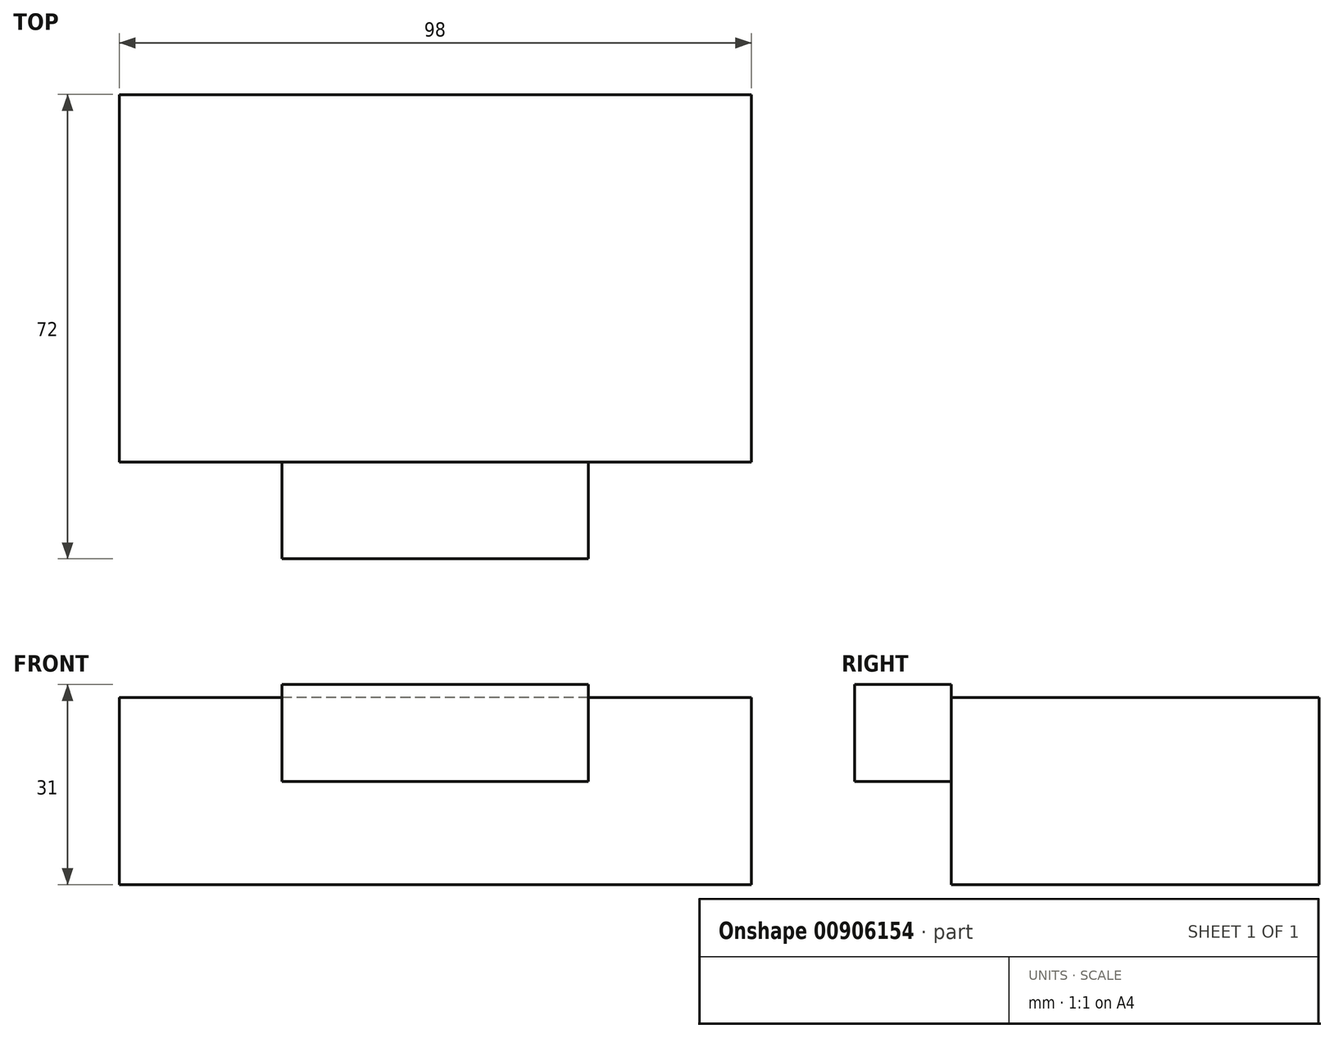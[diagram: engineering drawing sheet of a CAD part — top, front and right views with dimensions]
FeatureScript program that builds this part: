
annotation { "Feature Type Name" : "Feature", "Feature Type Description" : "" }
export const myFeature = defineFeature(function(context is Context, id is Id, definition is map)
    precondition{}
    {
        {
            var Q0;
            Q0=qCreatedBy(makeId("Top.planeOp"),FACE);
            var sketch = newSketch(context, id + "F0", { "sketchPlane" : qUnion([Q0])});
            skLineSegment(sketch, "E0.bottom", {"start": v(-39.14, -61.98) * mm, "end": v(-137.14, -61.98) * mm});
            skLineSegment(sketch, "E0.top", {"start": v(-39.14, -4.98) * mm, "end": v(-137.14, -4.98) * mm});
            skLineSegment(sketch, "E0.left", {"start": v(-39.14, -61.98) * mm, "end": v(-39.14, -4.98) * mm});
            skLineSegment(sketch, "E0.right", {"start": v(-137.14, -61.98) * mm, "end": v(-137.14, -4.98) * mm});
            skSolve(sketch);
        }
        {
            var Q0;
            Q0=makeQuery(id+"F0.imprint","IMPRINT",FACE,{"disambiguationData":[TD([[makeQuery(id+"F0.imprint","IMPRINT",EDGE,{"derivedFrom":sQuery(id+"F0.wireOp",EDGE,"E0.bottom")}),-1.0]])]});
            extrude(context, id + "F1", {"entities" : qUnion([Q0]), "depth" : 29 * mm, "offsetDistance" : 25 * mm});
        }
        {
            var Q0;
            Q0=makeQuery(id+"F1.opExtrude","SWEPT_FACE",FACE,{"disambiguationData":[OSD([sQuery(id+"F0.wireOp",EDGE,"E0.bottom")])]});
            var sketch = newSketch(context, id + "F2", { "sketchPlane" : qUnion([Q0])});
            skLineSegment(sketch, "E1", {"start": v(-111.9, 16) * mm, "end": v(-64.4, 16) * mm});
            skLineSegment(sketch, "E2", {"start": v(-64.4, 16) * mm, "end": v(-64.4, 31) * mm});
            skLineSegment(sketch, "E3", {"start": v(-64.4, 31) * mm, "end": v(-111.9, 31) * mm});
            skLineSegment(sketch, "E4", {"start": v(-111.9, 31) * mm, "end": v(-111.9, 16) * mm});
            skLineSegment(sketch, "E5", {"start": v(-88.14, 29) * mm, "end": v(-88.14, 0) * mm, "construction": true});
            skSolve(sketch);
        }
        {
            var Q0;
            Q0 = qSketchRegion(id + "F2", true);
            extrude(context, id + "F3", {"entities" : qUnion([Q0]), "operationType" : NewBodyOperationType.ADD, "depth" : 15 * mm, "offsetDistance" : 25 * mm});
        }
    });
